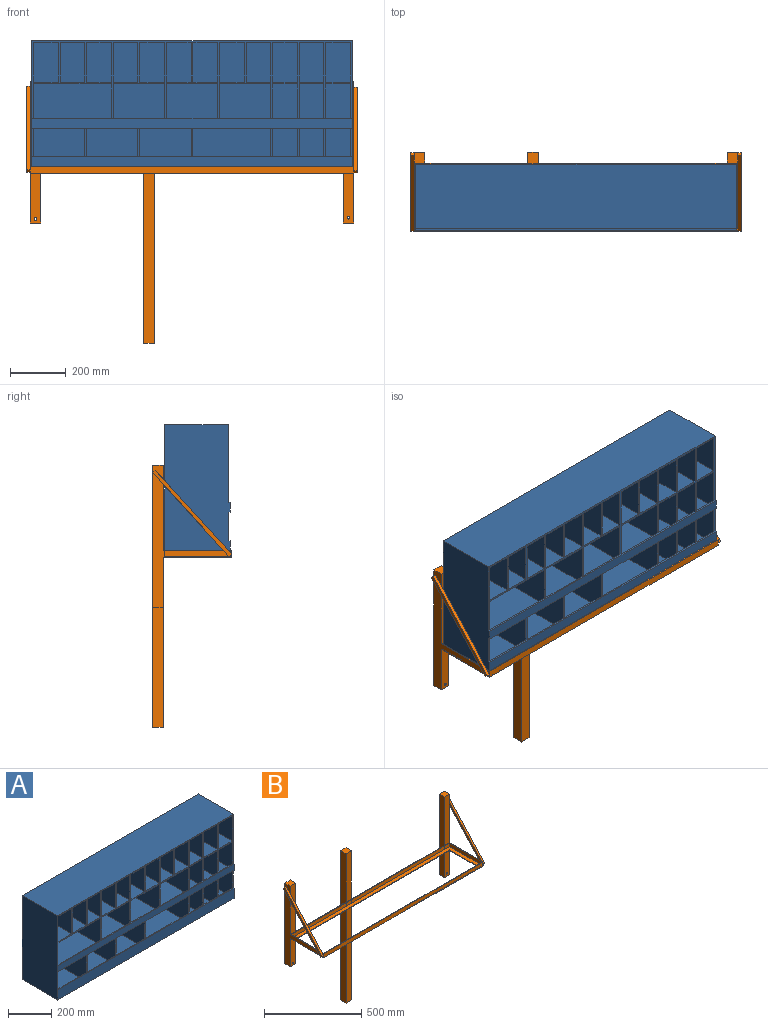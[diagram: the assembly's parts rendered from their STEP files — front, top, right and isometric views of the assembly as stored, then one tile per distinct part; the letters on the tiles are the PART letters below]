
ASSEMBLY  parts=2 mates=1
PART A: 156 faces, bbox 1149.4x235x473.1 mm
  f0: plane 1149.35x279.4mm, normal (0,-1,0), area 32681.4mm2, adj f9,f10,f11,f12,f13,f14,f15,f16
  f1: plane 101.6x6.35mm, normal (0,-1,0), area 645.2mm2, adj f56,f85,f110,f144
  f2: plane 101.6x6.35mm, normal (0,-1,0), area 645.2mm2, adj f55,f56,f105,f144
  f3: plane 101.6x6.35mm, normal (0,-1,0), area 645.2mm2, adj f56,f59,f100,f144
  f4: plane 101.6x6.35mm, normal (0,-1,0), area 645.2mm2, adj f56,f57,f62,f144
  f5: plane 101.6x6.35mm, normal (0,-1,0), area 645.2mm2, adj f56,f60,f65,f144
  f6: plane 101.6x6.35mm, normal (0,-1,0), area 645.2mm2, adj f56,f63,f68,f144
  f7: plane 101.6x6.35mm, normal (0,-1,0), area 645.2mm2, adj f56,f66,f83,f144
  f8: plane 101.6x6.35mm, normal (0,-1,0), area 645.2mm2, adj f56,f81,f108,f144
  f9: plane 222.25x152.4mm, normal (1,0,0), area 33870.9mm2, adj f0,f10,f106,f112,f155
  f10: plane 222.25x88.9mm, normal (0,0,-1), area 19758mm2, adj f0,f9,f11,f112
  f11: plane 222.25x152.4mm, normal (-1,0,0), area 33870.9mm2, adj f0,f10,f106,f112,f155
  f12: plane 222.25x152.4mm, normal (1,0,0), area 33870.9mm2, adj f0,f13,f86,f137,f147
  f13: plane 222.25x88.9mm, normal (0,0,-1), area 19758mm2, adj f0,f12,f14,f137
  f14: plane 222.25x152.4mm, normal (-1,0,0), area 33870.9mm2, adj f0,f13,f86,f137,f147
  f15: plane 222.25x152.4mm, normal (1,0,0), area 33870.9mm2, adj f0,f16,f87,f136,f148
  f16: plane 222.25x184.15mm, normal (0,0,-1), area 40927.3mm2, adj f0,f15,f17,f136
  f17: plane 222.25x152.4mm, normal (-1,0,0), area 33870.9mm2, adj f0,f16,f87,f136,f148
  f18: plane 222.25x152.4mm, normal (1,0,0), area 33870.9mm2, adj f0,f19,f88,f135,f149
  f19: plane 222.25x184.15mm, normal (0,0,-1), area 40927.3mm2, adj f0,f18,f20,f135
  f20: plane 222.25x152.4mm, normal (-1,0,0), area 33870.9mm2, adj f0,f19,f88,f135,f149
  f21: plane 222.25x152.4mm, normal (1,0,0), area 33870.9mm2, adj f0,f22,f89,f134,f150
  f22: plane 222.25x184.15mm, normal (0,0,-1), area 40927.3mm2, adj f0,f21,f23,f134
  f23: plane 222.25x152.4mm, normal (-1,0,0), area 33870.9mm2, adj f0,f22,f89,f134,f150
  f24: plane 222.25x142.88mm, normal (1,0,0), area 31754mm2, adj f0,f25,f90,f133
  f25: plane 222.25x88.9mm, normal (0,0,-1), area 19758mm2, adj f0,f24,f26,f133
  f26: plane 222.25x142.88mm, normal (-1,0,0), area 31754mm2, adj f0,f25,f90,f133
  f27: plane 222.25x88.9mm, normal (0,0,-1), area 19758mm2, adj f0,f28,f91,f132
  f28: plane 222.25x142.88mm, normal (-1,0,0), area 31754mm2, adj f0,f27,f29,f132
  f29: plane 222.25x88.9mm, normal (0,0,1), area 19758mm2, adj f0,f28,f91,f132
  f30: plane 222.25x88.9mm, normal (0,0,-1), area 19758mm2, adj f0,f31,f92,f131
  f31: plane 222.25x142.88mm, normal (-1,0,0), area 31754mm2, adj f0,f30,f32,f131
  f32: plane 222.25x88.9mm, normal (0,0,1), area 19758mm2, adj f0,f31,f92,f131
  f33: plane 222.25x88.9mm, normal (0,0,-1), area 19758mm2, adj f0,f34,f93,f130
  f34: plane 222.25x142.88mm, normal (-1,0,0), area 31754mm2, adj f0,f33,f35,f130
  f35: plane 222.25x88.9mm, normal (0,0,1), area 19758mm2, adj f0,f34,f93,f130
  f36: plane 222.25x88.9mm, normal (0,0,-1), area 19758mm2, adj f0,f37,f94,f129
  f37: plane 222.25x142.88mm, normal (-1,0,0), area 31754mm2, adj f0,f36,f38,f129
  f38: plane 222.25x88.9mm, normal (0,0,1), area 19758mm2, adj f0,f37,f94,f129
  f39: plane 222.25x88.9mm, normal (0,0,-1), area 19758mm2, adj f0,f40,f95,f128
  f40: plane 222.25x142.88mm, normal (-1,0,0), area 31754mm2, adj f0,f39,f41,f128
  f41: plane 222.25x88.9mm, normal (0,0,1), area 19758mm2, adj f0,f40,f95,f128
  f42: plane 222.25x88.9mm, normal (0,0,-1), area 19758mm2, adj f0,f43,f96,f127
  f43: plane 222.25x142.88mm, normal (-1,0,0), area 31754mm2, adj f0,f42,f44,f127
  f44: plane 222.25x88.9mm, normal (0,0,1), area 19758mm2, adj f0,f43,f96,f127
  f45: plane 222.25x88.9mm, normal (0,0,-1), area 19758mm2, adj f0,f46,f97,f126
  f46: plane 222.25x142.88mm, normal (-1,0,0), area 31754mm2, adj f0,f45,f47,f126
  f47: plane 222.25x88.9mm, normal (0,0,1), area 19758mm2, adj f0,f46,f97,f126
  f48: plane 222.25x88.9mm, normal (0,0,-1), area 19758mm2, adj f0,f49,f98,f125
  f49: plane 222.25x142.88mm, normal (-1,0,0), area 31754mm2, adj f0,f48,f50,f125
  f50: plane 222.25x88.9mm, normal (0,0,1), area 19758mm2, adj f0,f49,f98,f125
  f51: plane 222.25x88.9mm, normal (0,0,-1), area 19758mm2, adj f0,f52,f99,f124
  f52: plane 222.25x142.88mm, normal (-1,0,0), area 31754mm2, adj f0,f51,f53,f124
  f53: plane 222.25x88.9mm, normal (0,0,1), area 19758mm2, adj f0,f52,f99,f124
  f54: plane 222.25x184.15mm, normal (0,0,1), area 40927.3mm2, adj f55,f100,f123,f146
  f55: plane 222.25x152.4mm, normal (1,0,0), area 33870.9mm2, adj f2,f54,f56,f123,f146
  f56: plane 1149.35x228.6mm, normal (0,0,-1), area 251451.1mm2, adj f1,f2,f3,f4,f5,f6,f7,f8
  f57: plane 222.25x152.4mm, normal (-1,0,0), area 33870.9mm2, adj f4,f56,f58,f122,f142
  f58: plane 222.25x184.15mm, normal (0,0,1), area 40927.3mm2, adj f57,f59,f122,f142
  f59: plane 222.25x152.4mm, normal (1,0,0), area 33870.9mm2, adj f3,f56,f58,f122,f142
  f60: plane 222.25x152.4mm, normal (-1,0,0), area 33870.9mm2, adj f5,f56,f61,f121,f141
  f61: plane 279.4x222.25mm, normal (0,0,1), area 62096.6mm2, adj f60,f62,f121,f141
  f62: plane 222.25x152.4mm, normal (1,0,0), area 33870.9mm2, adj f4,f56,f61,f121,f141
  f63: plane 222.25x152.4mm, normal (-1,0,0), area 33870.9mm2, adj f6,f56,f64,f120,f139
  f64: plane 222.25x88.9mm, normal (0,0,1), area 19758mm2, adj f63,f65,f120,f139
  f65: plane 222.25x152.4mm, normal (1,0,0), area 33870.9mm2, adj f5,f56,f64,f120,f139
  f66: plane 222.25x152.4mm, normal (-1,0,0), area 33870.9mm2, adj f7,f56,f67,f119,f138
  f67: plane 222.25x88.9mm, normal (0,0,1), area 19758mm2, adj f66,f68,f119,f138
  f68: plane 222.25x152.4mm, normal (1,0,0), area 33870.9mm2, adj f6,f56,f67,f119,f138
  f69: plane 222.25x88.9mm, normal (0,0,1), area 19758mm2, adj f0,f70,f101,f118
  f70: plane 222.25x142.88mm, normal (1,0,0), area 31754mm2, adj f0,f69,f71,f118
  f71: plane 222.25x88.9mm, normal (0,0,-1), area 19758mm2, adj f0,f70,f101,f118
  f72: plane 279.4x222.25mm, normal (0,0,1), area 62096.7mm2, adj f73,f102,f117,f151
  f73: plane 222.25x152.4mm, normal (1,0,0), area 33870.9mm2, adj f0,f72,f74,f117,f151
  f74: plane 279.4x222.25mm, normal (0,0,-1), area 62096.7mm2, adj f0,f73,f102,f117
  f75: plane 222.25x152.4mm, normal (-1,0,0), area 33870.9mm2, adj f0,f76,f103,f116,f152
  f76: plane 222.25x88.9mm, normal (0,0,1), area 19758mm2, adj f75,f77,f116,f152
  f77: plane 222.25x152.4mm, normal (1,0,0), area 33870.9mm2, adj f0,f76,f103,f116,f152
  f78: plane 222.25x88.9mm, normal (0,0,-1), area 19758mm2, adj f0,f79,f104,f115
  f79: plane 222.25x142.88mm, normal (-1,0,0), area 31754mm2, adj f0,f78,f80,f115
  f80: plane 222.25x88.9mm, normal (0,0,1), area 19758mm2, adj f0,f79,f104,f115
  f81: plane 222.25x152.4mm, normal (-1,0,0), area 33870.9mm2, adj f8,f56,f82,f114,f140
  f82: plane 222.25x88.9mm, normal (0,0,1), area 19758mm2, adj f81,f83,f114,f140
  f83: plane 222.25x152.4mm, normal (1,0,0), area 33870.9mm2, adj f7,f56,f82,f114,f140
  f84: plane 222.25x184.15mm, normal (0,0,1), area 40927.3mm2, adj f85,f105,f113,f143
  f85: plane 222.25x152.4mm, normal (1,0,0), area 33870.9mm2, adj f1,f56,f84,f113,f143
  f86: plane 222.25x88.9mm, normal (0,0,1), area 19758mm2, adj f12,f14,f137,f147
  f87: plane 222.25x184.15mm, normal (0,0,1), area 40927.3mm2, adj f15,f17,f136,f148
  f88: plane 222.25x184.15mm, normal (0,0,1), area 40927.3mm2, adj f18,f20,f135,f149
  f89: plane 222.25x184.15mm, normal (0,0,1), area 40927.3mm2, adj f21,f23,f134,f150
  f90: plane 222.25x88.9mm, normal (0,0,1), area 19758mm2, adj f0,f24,f26,f133
  f91: plane 222.25x142.88mm, normal (1,0,0), area 31754mm2, adj f0,f27,f29,f132
  f92: plane 222.25x142.88mm, normal (1,0,0), area 31754mm2, adj f0,f30,f32,f131
  f93: plane 222.25x142.88mm, normal (1,0,0), area 31754mm2, adj f0,f33,f35,f130
  f94: plane 222.25x142.88mm, normal (1,0,0), area 31754mm2, adj f0,f36,f38,f129
  f95: plane 222.25x142.88mm, normal (1,0,0), area 31754mm2, adj f0,f39,f41,f128
  f96: plane 222.25x142.88mm, normal (1,0,0), area 31754mm2, adj f0,f42,f44,f127
  f97: plane 222.25x142.88mm, normal (1,0,0), area 31754mm2, adj f0,f45,f47,f126
  f98: plane 222.25x142.88mm, normal (1,0,0), area 31754mm2, adj f0,f48,f50,f125
  f99: plane 222.25x142.88mm, normal (1,0,0), area 31754mm2, adj f0,f51,f53,f124
  f100: plane 222.25x152.4mm, normal (-1,0,0), area 33870.9mm2, adj f3,f54,f56,f123,f146
  f101: plane 222.25x142.88mm, normal (-1,0,0), area 31754mm2, adj f0,f69,f71,f118
  f102: plane 222.25x152.4mm, normal (-1,0,0), area 33870.9mm2, adj f0,f72,f74,f117,f151
  f103: plane 222.25x88.9mm, normal (0,0,-1), area 19758mm2, adj f0,f75,f77,f116
  f104: plane 222.25x142.88mm, normal (1,0,0), area 31754mm2, adj f0,f78,f80,f115
  f105: plane 222.25x152.4mm, normal (-1,0,0), area 33870.9mm2, adj f2,f56,f84,f113,f143
  f106: plane 222.25x88.9mm, normal (0,0,1), area 19758mm2, adj f9,f11,f112,f155
  f107: plane 1149.35x234.95mm, normal (0,0,-1), area 270039.8mm2, adj f108,f110,f111,f145
  f108: plane 473.08x234.95mm, normal (1,0,0), area 108729.6mm2, adj f0,f8,f56,f107,f109,f111,f144,f145
  f109: plane 1149.35x228.6mm, normal (0,0,1), area 262741.4mm2, adj f0,f108,f110,f111
  f110: plane 473.08x234.95mm, normal (-1,0,0), area 108729.6mm2, adj f0,f1,f56,f107,f109,f111,f144,f145
  f111: plane 1149.35x473.08mm, normal (0,1,0), area 543728.8mm2, adj f107,f108,f109,f110
  f112: plane 152.4x88.9mm, normal (0,-1,0), area 13548.4mm2, adj f9,f10,f11,f106
  f113: plane 184.15x152.4mm, normal (0,-1,0), area 28064.5mm2, adj f56,f84,f85,f105
  f114: plane 152.4x88.9mm, normal (0,-1,0), area 13548.4mm2, adj f56,f81,f82,f83
  f115: plane 142.88x88.9mm, normal (0,-1,0), area 12701.6mm2, adj f78,f79,f80,f104
  f116: plane 152.4x88.9mm, normal (0,-1,0), area 13548.4mm2, adj f75,f76,f77,f103
  f117: plane 279.4x152.4mm, normal (0,-1,0), area 42580.6mm2, adj f72,f73,f74,f102
  f118: plane 142.88x88.9mm, normal (0,-1,0), area 12701.6mm2, adj f69,f70,f71,f101
  f119: plane 152.4x88.9mm, normal (0,-1,0), area 13548.4mm2, adj f56,f66,f67,f68
  f120: plane 152.4x88.9mm, normal (0,-1,0), area 13548.4mm2, adj f56,f63,f64,f65
  f121: plane 279.4x152.4mm, normal (0,-1,0), area 42580.6mm2, adj f56,f60,f61,f62
  f122: plane 184.15x152.4mm, normal (0,-1,0), area 28064.5mm2, adj f56,f57,f58,f59
  f123: plane 184.15x152.4mm, normal (0,-1,0), area 28064.5mm2, adj f54,f55,f56,f100
  f124: plane 142.88x88.9mm, normal (0,-1,0), area 12701.6mm2, adj f51,f52,f53,f99
  f125: plane 142.88x88.9mm, normal (0,-1,0), area 12701.6mm2, adj f48,f49,f50,f98
  f126: plane 142.88x88.9mm, normal (0,-1,0), area 12701.6mm2, adj f45,f46,f47,f97
  f127: plane 142.88x88.9mm, normal (0,-1,0), area 12701.6mm2, adj f42,f43,f44,f96
  f128: plane 142.88x88.9mm, normal (0,-1,0), area 12701.6mm2, adj f39,f40,f41,f95
  f129: plane 142.88x88.9mm, normal (0,-1,0), area 12701.6mm2, adj f36,f37,f38,f94
  f130: plane 142.88x88.9mm, normal (0,-1,0), area 12701.6mm2, adj f33,f34,f35,f93
  f131: plane 142.88x88.9mm, normal (0,-1,0), area 12701.6mm2, adj f30,f31,f32,f92
  f132: plane 142.88x88.9mm, normal (0,-1,0), area 12701.6mm2, adj f27,f28,f29,f91
  f133: plane 142.88x88.9mm, normal (0,-1,0), area 12701.6mm2, adj f24,f25,f26,f90
  f134: plane 184.15x152.4mm, normal (0,-1,0), area 28064.5mm2, adj f21,f22,f23,f89
  f135: plane 184.15x152.4mm, normal (0,-1,0), area 28064.5mm2, adj f18,f19,f20,f88
  f136: plane 184.15x152.4mm, normal (0,-1,0), area 28064.5mm2, adj f15,f16,f17,f87
  f137: plane 152.4x88.9mm, normal (0,-1,0), area 13548.4mm2, adj f12,f13,f14,f86
  f138: plane 88.9x50.8mm, normal (0,1,0), area 4516.1mm2, adj f66,f67,f68,f144
  f139: plane 88.9x50.8mm, normal (0,1,0), area 4516.1mm2, adj f63,f64,f65,f144
  f140: plane 88.9x50.8mm, normal (0,1,0), area 4516.1mm2, adj f81,f82,f83,f144
  f141: plane 279.4x50.8mm, normal (0,1,0), area 14193.5mm2, adj f60,f61,f62,f144
  f142: plane 184.15x50.8mm, normal (0,1,0), area 9354.8mm2, adj f57,f58,f59,f144
  f143: plane 184.15x50.8mm, normal (0,1,0), area 9354.8mm2, adj f84,f85,f105,f144
  f144: plane 1149.35x6.35mm, normal (0,0,1), area 7298.4mm2, adj f1,f2,f3,f4,f5,f6,f7,f8
  f145: plane 1149.35x57.15mm, normal (0,-1,0), area 65685.4mm2, adj f107,f108,f110,f144
  f146: plane 184.15x50.8mm, normal (0,1,0), area 9354.8mm2, adj f54,f55,f100,f144
  f147: plane 88.9x28.58mm, normal (0,1,0), area 2540.3mm2, adj f12,f14,f86,f153
  f148: plane 184.15x28.58mm, normal (0,1,0), area 5262.1mm2, adj f15,f17,f87,f153
  f149: plane 184.15x28.58mm, normal (0,1,0), area 5262.1mm2, adj f18,f20,f88,f153
  f150: plane 184.15x28.58mm, normal (0,1,0), area 5262.1mm2, adj f21,f23,f89,f153
  f151: plane 279.4x28.58mm, normal (0,1,0), area 7983.9mm2, adj f72,f73,f102,f153
  f152: plane 88.9x28.58mm, normal (0,1,0), area 2540.3mm2, adj f75,f76,f77,f153
  f153: plane 1149.35x6.35mm, normal (0,0,1), area 7298.4mm2, adj f0,f108,f110,f147,f148,f149,f150,f151
  f154: plane 1149.35x34.93mm, normal (0,-1,0), area 40141mm2, adj f56,f108,f110,f153
  f155: plane 88.9x28.58mm, normal (0,1,0), area 2540.3mm2, adj f9,f11,f106,f153
PART B: 53 faces, bbox 1184.3x282.6x939.8 mm
  f0: plane 12.7x11.57mm, normal (-1,0,0), area 73.4mm2, adj f8,f19,f48
  f1: plane 481.92x282.58mm, normal (-1,0,0), area 23408.7mm2, adj f8,f14,f19,f20,f23,f24,f25,f50
  f2: plane 49.08x38.1mm, normal (-1,0,0), area 1165.1mm2, adj f21,f24,f25,f48,f49
  f3: plane 478.52x282.58mm, normal (1,0,0), area 23202.9mm2, adj f8,f14,f19,f33,f36,f37,f38,f44
  f4: plane 52.39x38.1mm, normal (1,0,0), area 1293mm2, adj f35,f37,f38,f42,f43
  f5: plane 15.3x13.97mm, normal (1,0,0), area 106.9mm2, adj f8,f19,f43
  f6: plane 676.28x25.4mm, normal (0,1,0), area 17177.4mm2, adj f14,f19,f29,f34
  f7: plane 368.3x25.4mm, normal (0,1,0), area 9354.8mm2, adj f14,f19,f22,f27
  f8: plane 1158.88x25.4mm, normal (0,-1,0), area 29435.4mm2, adj f0,f1,f3,f5,f14,f19
  f9: plane 193.68x3.18mm, normal (-1,0,0), area 614.9mm2, adj f10,f12,f13,f14
  f10: plane 1108.08x3.18mm, normal (0,1,0), area 3518.1mm2, adj f9,f11,f13,f14
  f11: plane 193.68x3.18mm, normal (1,0,0), area 614.9mm2, adj f10,f12,f13,f14
  f12: plane 1108.08x3.18mm, normal (0,-1,0), area 3518.1mm2, adj f9,f11,f13,f14
  f13: plane 1152.53x238.13mm, normal (0,0,1), area 59838.6mm2, adj f9,f10,f11,f12,f15,f16,f17,f18
  f14: plane 1158.88x244.48mm, normal (0,0,-1), area 68709.5mm2, adj f1,f3,f6,f7,f8,f9,f10,f11
  f15: plane 1152.53x22.23mm, normal (0,1,0), area 25614.9mm2, adj f13,f16,f18,f19
  f16: plane 238.13x22.23mm, normal (1,0,0), area 5292.3mm2, adj f13,f15,f17,f19
  f17: plane 1152.53x22.23mm, normal (0,-1,0), area 25614.9mm2, adj f13,f16,f18,f19
  f18: plane 238.13x22.23mm, normal (-1,0,0), area 5292.3mm2, adj f13,f15,f17,f19
  f19: plane 1158.88x244.48mm, normal (0,0,1), area 8871mm2, adj f0,f1,f3,f5,f6,f7,f8,f15
  f20: plane 177.8x38.1mm, normal (0,-1,0), area 6702.9mm2, adj f1,f14,f22,f23,f40
  f21: plane 38.1x38.1mm, normal (0,0,1), area 1451.6mm2, adj f2,f22,f24,f25
  f22: plane 508x38.1mm, normal (1,0,0), area 19354.8mm2, adj f7,f20,f21,f23,f24,f25
  f23: plane 38.1x38.1mm, normal (0,0,-1), area 1451.6mm2, adj f1,f20,f22,f24
  f24: plane 508x38.1mm, normal (0,1,0), area 19283.5mm2, adj f1,f2,f21,f22,f23,f40
  f25: plane 304.8x38.1mm, normal (0,-1,0), area 11612.9mm2, adj f1,f2,f19,f21,f22,f47
  f26: plane 609.6x38.1mm, normal (0,-1,0), area 23225.8mm2, adj f14,f27,f29,f30
  f27: plane 939.8x38.1mm, normal (-1,0,0), area 35806.4mm2, adj f7,f26,f28,f30,f31,f32
  f28: plane 38.1x38.1mm, normal (0,0,1), area 1451.6mm2, adj f27,f29,f31,f32
  f29: plane 939.8x38.1mm, normal (1,0,0), area 35806.4mm2, adj f6,f26,f28,f30,f31,f32
  f30: plane 38.1x38.1mm, normal (0,0,-1), area 1451.6mm2, adj f26,f27,f29,f31
  f31: plane 939.8x38.1mm, normal (0,1,0), area 35806.4mm2, adj f27,f28,f29,f30
  f32: plane 304.8x38.1mm, normal (0,-1,0), area 11612.9mm2, adj f19,f27,f28,f29
  f33: plane 177.8x38.1mm, normal (0,-1,0), area 6702.9mm2, adj f3,f14,f34,f36,f39
  f34: plane 508x38.1mm, normal (-1,0,0), area 19354.8mm2, adj f6,f33,f35,f36,f37,f38
  f35: plane 38.1x38.1mm, normal (0,0,1), area 1451.6mm2, adj f4,f34,f37,f38
  f36: plane 38.1x38.1mm, normal (0,0,-1), area 1451.6mm2, adj f3,f33,f34,f37
  f37: plane 508x38.1mm, normal (0,1,0), area 19283.5mm2, adj f3,f4,f34,f35,f36,f39
  f38: plane 304.8x38.1mm, normal (0,-1,0), area 11612.9mm2, adj f3,f4,f19,f34,f35,f41
  f39: cylinder r=4.76mm len=38.1mm, axis (0,1,0), area 1140.1mm2, adj f33,f37
  f40: cylinder r=4.76mm len=38.1mm, axis (0,1,0), area 1140.1mm2, adj f20,f24
  f41: plane 252.41x230.5mm, normal (-1,0,0), area 4177.1mm2, adj f19,f38,f43,f45
  f42: plane 12.7x9.77mm, normal (0,0.64,0.77), area 161.3mm2, adj f4,f43,f45,f46
  f43: plane 298.73x272.8mm, normal (0,-0.74,0.67), area 5137.8mm2, adj f4,f5,f41,f42,f44,f46
  f44: plane 12.7x9.38mm, normal (0,-0.67,-0.74), area 161.3mm2, adj f3,f43,f45,f46
  f45: plane 299.19x273.2mm, normal (0,0.74,-0.67), area 5145.5mm2, adj f3,f41,f42,f44,f46
  f46: plane 307.3x282.58mm, normal (1,0,0), area 5138.7mm2, adj f42,f43,f44,f45
  f47: plane 255.72x232.91mm, normal (1,0,0), area 4228.7mm2, adj f19,f25,f48,f50
  f48: plane 299.51x272.79mm, normal (0,-0.74,0.67), area 5145mm2, adj f0,f2,f47,f49,f51,f52
  f49: plane 12.7x9.79mm, normal (0,0.64,0.77), area 161.3mm2, adj f2,f48,f50,f52
  f50: plane 299.97x273.19mm, normal (0,0.74,-0.67), area 5152.7mm2, adj f1,f47,f49,f51,f52
  f51: plane 12.7x9.39mm, normal (0,-0.67,-0.74), area 161.3mm2, adj f1,f48,f50,f52
  f52: plane 308.06x282.58mm, normal (-1,0,0), area 5145.9mm2, adj f48,f49,f50,f51
PLACE A t=(-10.9,78.1,199.62)mm
PLACE B t=(-10.9,-39.37,-40.09)mm
MATE fastened A.f107 <-> B.f13  axis (0,0,-1) through (563.77,78.1,-36.91)mm
